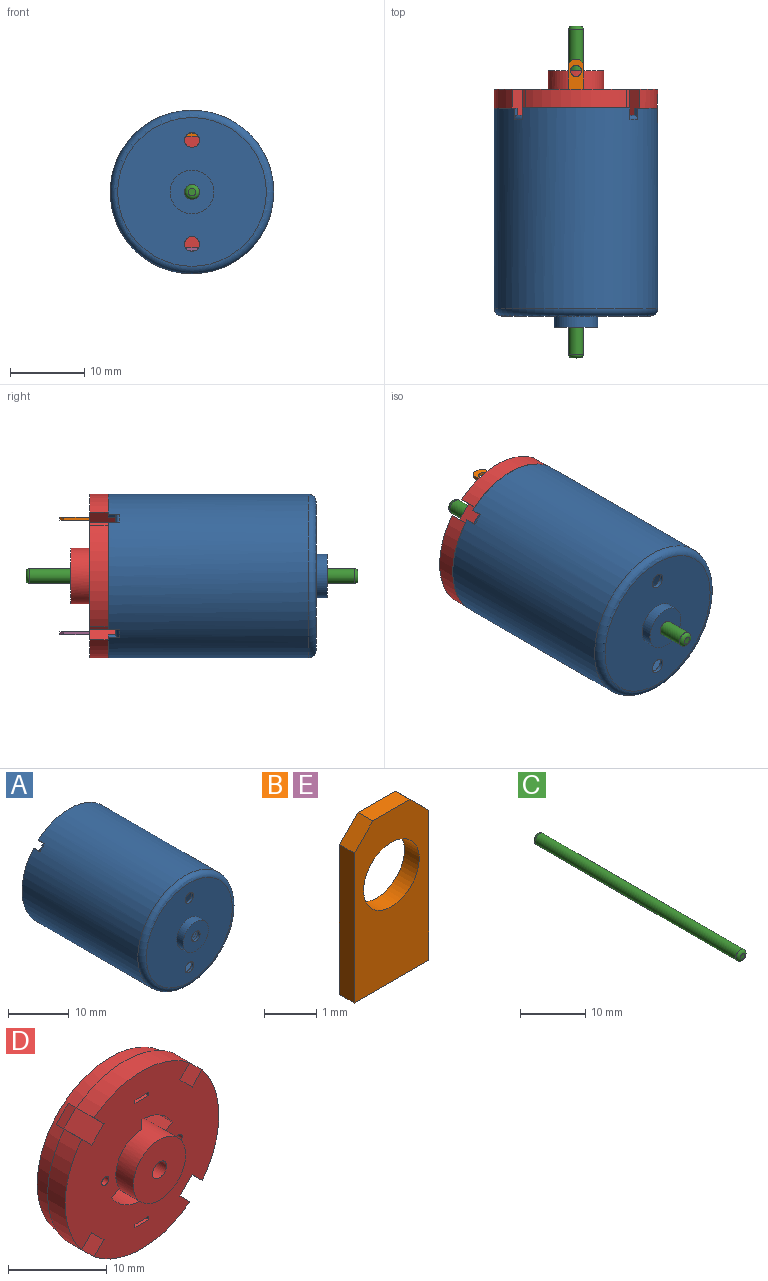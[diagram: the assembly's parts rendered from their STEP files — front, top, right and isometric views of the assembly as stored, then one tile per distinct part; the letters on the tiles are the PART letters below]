
ASSEMBLY  parts=5 mates=5
PART A: 52 faces, bbox 23.8x29.5x23.8 mm
  f0: plane 1.52x0.37mm, normal (0.71,0,-0.71), area 0.6mm2, adj f6,f7,f10,f49
  f1: plane 1.52x0.37mm, normal (-0.71,0,-0.71), area 0.6mm2, adj f6,f9,f10,f50
  f2: plane 1.52x0.37mm, normal (0.71,0,0.71), area 0.6mm2, adj f6,f10,f12,f51
  f3: plane 1.52x0.37mm, normal (-0.71,0,0.71), area 0.6mm2, adj f5,f6,f10,f48
  f4: plane 1.52x0.37mm, normal (0.71,0,-0.71), area 0.6mm2, adj f6,f9,f10,f48
  f5: plane 6.23x3.02mm, normal (0,1,0), area 3.3mm2, adj f3,f6,f10,f25
  f6: cylinder r=10.5mm len=27.5mm, axis (0,1,0), area 1801.3mm2, adj f0,f1,f2,f3,f4,f5,f7,f8
  f7: plane 14.46x3.06mm, normal (0,1,0), area 7.7mm2, adj f0,f6,f10,f24
  f8: plane 6.23x3.02mm, normal (0,1,0), area 3.3mm2, adj f6,f10,f23,f26
  f9: plane 14.46x3.06mm, normal (0,1,0), area 7.7mm2, adj f1,f4,f6,f10
  f10: cylinder r=11mm len=27mm, axis (0,1,0), area 1853.1mm2, adj f0,f1,f2,f3,f4,f5,f7,f8
  f11: plane 20x20mm, normal (0,-1,0), area 280.5mm2, adj f13,f19,f20,f21
  f12: plane 14.46x3.06mm, normal (0,1,0), area 7.7mm2, adj f2,f6,f10,f22
  f13: cylinder r=2.95mm len=5.9mm, axis (0,1,0), area 27.8mm2, adj f11,f14
  f14: plane 5.9x5.9mm, normal (0,-1,0), area 24.2mm2, adj f13,f18
  f15: plane 21x21mm, normal (0,1,0), area 321.2mm2, adj f6,f16,f19,f20
  f16: cylinder r=2.45mm len=4.9mm, axis (0,1,0), area 23.1mm2, adj f15,f17
  f17: plane 4.9x4.9mm, normal (0,1,0), area 15.7mm2, adj f16,f18
  f18: cylinder r=1mm len=2mm, axis (0,-1,0), area 3.1mm2, adj f14,f17
  f19: cylinder r=1mm len=2mm, axis (0,-1,0), area 3.1mm2, adj f11,f15
  f20: cylinder r=1mm len=2mm, axis (0,-1,0), area 3.1mm2, adj f11,f15
  f21: torus R=10mm, axis (0,-1,0), area 105mm2, adj f10,f11
  f22: plane 1.52x0.37mm, normal (-0.71,0,0.71), area 0.6mm2, adj f6,f10,f12,f49
  f23: plane 1.52x0.37mm, normal (-0.71,0,-0.71), area 0.6mm2, adj f6,f8,f10,f51
  f24: plane 1.52x0.37mm, normal (0.71,0,0.71), area 0.6mm2, adj f6,f7,f10,f50
  f25: plane 2x0.5mm, normal (0,0,-1), area 1mm2, adj f5,f6,f10,f27
  f26: plane 2x0.5mm, normal (0,0,1), area 1mm2, adj f6,f8,f10,f27
  f27: plane 2x0.55mm, normal (0,1,0), area 1mm2, adj f6,f10,f25,f26
  f28: plane 1.41x1.41mm, normal (0,-1,0), area 0.8mm2, adj f6,f29,f30,f31
  f29: plane 0.5x0.35mm, normal (0.71,0,-0.71), area 0.2mm2, adj f6,f28,f30,f32
  f30: plane 1.06x1.06mm, normal (-0.71,0,-0.71), area 0.7mm2, adj f28,f29,f31,f32
  f31: plane 0.5x0.35mm, normal (-0.71,0,0.71), area 0.2mm2, adj f6,f28,f30,f32
  f32: plane 1.41x1.41mm, normal (0,1,0), area 0.8mm2, adj f29,f30,f31,f48
  f33: plane 1.41x1.41mm, normal (0,-1,0), area 0.8mm2, adj f6,f34,f35,f36
  f34: plane 0.5x0.35mm, normal (-0.71,0,-0.71), area 0.2mm2, adj f6,f33,f35,f37
  f35: plane 1.06x1.06mm, normal (-0.71,0,0.71), area 0.7mm2, adj f33,f34,f36,f37
  f36: plane 0.5x0.35mm, normal (0.71,0,0.71), area 0.2mm2, adj f6,f33,f35,f37
  f37: plane 1.41x1.41mm, normal (0,1,0), area 0.8mm2, adj f34,f35,f36,f51
  f38: plane 1.41x1.41mm, normal (0,-1,0), area 0.8mm2, adj f6,f39,f40,f41
  f39: plane 0.5x0.35mm, normal (0.71,0,0.71), area 0.2mm2, adj f6,f38,f40,f42
  f40: plane 1.06x1.06mm, normal (0.71,0,-0.71), area 0.7mm2, adj f38,f39,f41,f42
  f41: plane 0.5x0.35mm, normal (-0.71,0,-0.71), area 0.2mm2, adj f6,f38,f40,f42
  f42: plane 1.41x1.41mm, normal (0,1,0), area 0.8mm2, adj f39,f40,f41,f50
  f43: plane 1.41x1.41mm, normal (0,-1,0), area 0.8mm2, adj f6,f44,f45,f46
  f44: plane 0.5x0.35mm, normal (-0.71,0,0.71), area 0.2mm2, adj f6,f43,f45,f47
  f45: plane 1.06x1.06mm, normal (0.71,0,0.71), area 0.7mm2, adj f43,f44,f46,f47
  f46: plane 0.5x0.35mm, normal (0.71,0,-0.71), area 0.2mm2, adj f6,f43,f45,f47
  f47: plane 1.41x1.41mm, normal (0,1,0), area 0.8mm2, adj f44,f45,f46,f49
  f48: torus R=10.5mm, axis (0,1,0), area 1.2mm2, adj f3,f4,f10,f32
  f49: torus R=10.5mm, axis (0,1,0), area 1.2mm2, adj f0,f10,f22,f47
  f50: torus R=10.5mm, axis (0,1,0), area 1.2mm2, adj f1,f10,f24,f42
  f51: torus R=10.5mm, axis (0,1,0), area 1.2mm2, adj f2,f10,f23,f37
PART B: 9 faces, bbox 2x0.4x4 mm
  f0: plane 3.5x0.4mm, normal (1,0,0), area 1.4mm2, adj f3,f5,f6,f8
  f1: plane 1x0.4mm, normal (0,0,1), area 0.4mm2, adj f5,f6,f7,f8
  f2: plane 3.5x0.4mm, normal (-1,0,0), area 1.4mm2, adj f3,f5,f6,f7
  f3: plane 2x0.4mm, normal (0,0,-1), area 0.8mm2, adj f0,f2,f5,f6
  f4: cylinder r=0.75mm len=1.5mm, axis (0,1,0), area 1.9mm2, adj f5,f6
  f5: plane 4x2mm, normal (0,-1,0), area 6mm2, adj f0,f1,f2,f3,f4,f7,f8
  f6: plane 4x2mm, normal (0,1,0), area 6mm2, adj f0,f1,f2,f3,f4,f7,f8
  f7: plane 0.5x0.5mm, normal (-0.71,0,0.71), area 0.3mm2, adj f1,f2,f5,f6
  f8: plane 0.5x0.5mm, normal (0.71,0,0.71), area 0.3mm2, adj f0,f1,f5,f6
PART C: 5 faces, bbox 2.2x44.7x2.2 mm
  f0: cylinder r=1mm len=43.7mm, axis (0,1,0), area 274.6mm2, adj f3,f4
  f1: plane 1x1mm, normal (0,-1,0), area 0.8mm2, adj f4
  f2: plane 1x1mm, normal (0,1,0), area 0.8mm2, adj f3
  f3: torus R=0.5mm, axis (0,-1,0), area 4mm2, adj f0,f2
  f4: torus R=0.5mm, axis (0,-1,0), area 4mm2, adj f0,f1
PART D: 49 faces, bbox 22x7x22 mm
  f0: cylinder r=11mm len=13.69mm, axis (0,1,0), area 36.9mm2, adj f3,f5,f38,f46
  f1: cylinder r=11mm len=13.69mm, axis (0,1,0), area 36.9mm2, adj f3,f6,f34,f41
  f2: cylinder r=11mm len=13.69mm, axis (0,1,0), area 40.9mm2, adj f3,f7,f8,f30,f31,f32,f37,f42
  f3: plane 22x22mm, normal (0,-1,0), area 300.9mm2, adj f0,f1,f2,f10,f11,f12,f13,f14
  f4: plane 13.69x2.74mm, normal (0,1,0), area 7.2mm2, adj f9,f22,f33,f45
  f5: plane 13.69x2.74mm, normal (0,1,0), area 7.2mm2, adj f0,f9,f38,f46
  f6: plane 13.69x2.74mm, normal (0,1,0), area 7.2mm2, adj f1,f9,f34,f41
  f7: plane 5.84x2.7mm, normal (0,1,0), area 3.1mm2, adj f2,f9,f30,f42
  f8: plane 5.84x2.7mm, normal (0,1,0), area 3.1mm2, adj f2,f9,f31,f37
  f9: cylinder r=10.5mm len=21mm, axis (0,-1,0), area 112.9mm2, adj f4,f5,f6,f7,f8,f30,f31,f32
  f10: plane 4.5x2mm, normal (0,0,1), area 9mm2, adj f3,f11,f21,f32
  f11: plane 4.5x0.4mm, normal (1,0,0), area 1.8mm2, adj f3,f10,f12,f32
  f12: plane 4.5x2mm, normal (0,0,-1), area 9mm2, adj f3,f11,f21,f32
  f13: plane 4.5x1.25mm, normal (-1,0,0), area 5.6mm2, adj f3,f14,f19,f32
  f14: cylinder r=5mm len=4.5mm, axis (0,1,0), area 23.6mm2, adj f3,f13,f25,f32
  f15: plane 4.5x0.4mm, normal (1,0,0), area 1.8mm2, adj f3,f16,f26,f32
  f16: plane 4.5x2mm, normal (0,0,-1), area 9mm2, adj f3,f15,f17,f32
  f17: plane 4.5x0.4mm, normal (-1,0,0), area 1.8mm2, adj f3,f16,f26,f32
  f18: plane 4.5x1.08mm, normal (-0.5,0,0.87), area 5.6mm2, adj f3,f19,f27,f32
  f19: cylinder r=3.75mm len=7.5mm, axis (0,1,0), area 94.2mm2, adj f3,f13,f18,f20,f25,f29,f32
  f20: plane 4.5x1.25mm, normal (1,0,0), area 5.6mm2, adj f3,f19,f27,f32
  f21: plane 4.5x0.4mm, normal (-1,0,0), area 1.8mm2, adj f3,f10,f12,f32
  f22: cylinder r=11mm len=13.69mm, axis (0,1,0), area 36.9mm2, adj f3,f4,f33,f45
  f23: cylinder r=0.5mm len=4.5mm, axis (0,1,0), area 14.1mm2, adj f3,f32
  f24: cylinder r=0.5mm len=4.5mm, axis (0,1,0), area 14.1mm2, adj f3,f32
  f25: plane 4.5x1.08mm, normal (0.5,0,-0.87), area 5.6mm2, adj f3,f14,f19,f32
  f26: plane 4.5x2mm, normal (0,0,1), area 9mm2, adj f3,f15,f17,f32
  f27: cylinder r=5mm len=4.5mm, axis (0,1,0), area 23.6mm2, adj f3,f18,f20,f32
  f28: cylinder r=1mm len=7mm, axis (0,1,0), area 44mm2, adj f29,f32
  f29: plane 7.5x7.5mm, normal (0,-1,0), area 41mm2, adj f19,f28
  f30: plane 2x0.5mm, normal (0,0,1), area 1mm2, adj f2,f7,f9,f32
  f31: plane 2x0.5mm, normal (0,0,-1), area 1mm2, adj f2,f8,f9,f32
  f32: plane 21.5x21mm, normal (0,1,0), area 329.6mm2, adj f2,f9,f10,f11,f12,f13,f14,f15
  f33: plane 4x1.41mm, normal (0.71,0,0.71), area 7.2mm2, adj f3,f4,f9,f22,f35,f36
  f34: plane 4x1.41mm, normal (-0.71,0,-0.71), area 7.2mm2, adj f1,f3,f6,f9,f35,f36
  f35: plane 2.83x2.83mm, normal (0,-1,0), area 3.9mm2, adj f9,f33,f34,f36
  f36: plane 4x1.77mm, normal (-0.71,0,0.71), area 10mm2, adj f3,f33,f34,f35
  f37: plane 4x1.41mm, normal (-0.71,0,-0.71), area 7.2mm2, adj f2,f3,f8,f9,f39,f40
  f38: plane 4x1.41mm, normal (0.71,0,0.71), area 7.2mm2, adj f0,f3,f5,f9,f39,f40
  f39: plane 2.83x2.83mm, normal (0,-1,0), area 3.9mm2, adj f9,f37,f38,f40
  f40: plane 4x1.77mm, normal (0.71,0,-0.71), area 10mm2, adj f3,f37,f38,f39
  f41: plane 4x1.41mm, normal (0.71,0,-0.71), area 7.2mm2, adj f1,f3,f6,f9,f43,f44
  f42: plane 4x1.41mm, normal (-0.71,0,0.71), area 7.2mm2, adj f2,f3,f7,f9,f43,f44
  f43: plane 2.83x2.83mm, normal (0,-1,0), area 3.9mm2, adj f9,f41,f42,f44
  f44: plane 4x1.77mm, normal (0.71,0,0.71), area 10mm2, adj f3,f41,f42,f43
  f45: plane 4x1.41mm, normal (0.71,0,-0.71), area 7.2mm2, adj f3,f4,f9,f22,f47,f48
  f46: plane 4x1.41mm, normal (-0.71,0,0.71), area 7.2mm2, adj f0,f3,f5,f9,f47,f48
  f47: plane 2.83x2.83mm, normal (0,-1,0), area 3.9mm2, adj f9,f45,f46,f48
  f48: plane 4x1.77mm, normal (-0.71,0,-0.71), area 10mm2, adj f3,f45,f46,f47
PART E: same geometry as B
PLACE A at identity fixed
PLACE B rot(axis=(-1,0,0),90deg) t=(0,4.5,7.5)mm
PLACE C t=(0,11.05,0)mm
PLACE D rot(axis=(1,0,0),180deg) t=(0,0,0)mm
PLACE E rot(axis=(-1,0,0),90deg) t=(0,4.5,-7.9)mm
MATE slider A.f6 <-> D.f9  axis (0,1,0) through (0,-13.5,0)mm
MATE planar D.f7 <-> A.f5  axis (0,-1,0) through (9.84,0,-3.94)mm
MATE planar E.f3 <-> D.f3  axis (0,-1,0) through (0,2.5,-7.7)mm
MATE revolute C.f0 <-> A.f18  axis (0,-1,0) through (0,-33.5,0)mm
MATE planar B.f3 <-> D.f3  axis (0,-1,0) through (0,2.5,7.7)mm
